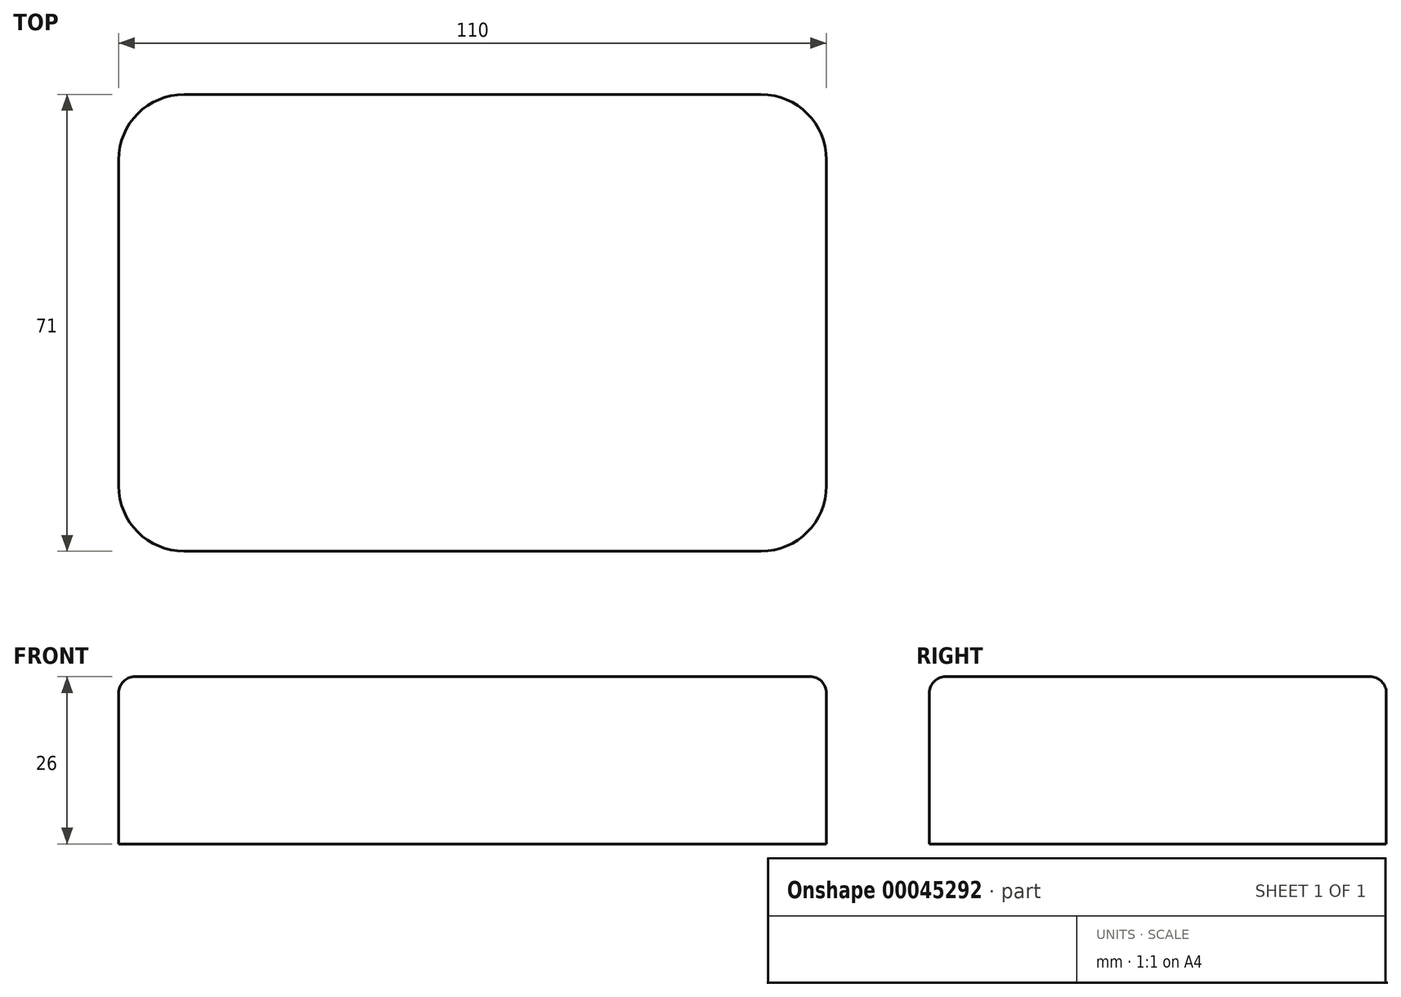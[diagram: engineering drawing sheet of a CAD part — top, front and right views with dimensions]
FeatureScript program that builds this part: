
annotation { "Feature Type Name" : "Feature", "Feature Type Description" : "" }
export const myFeature = defineFeature(function(context is Context, id is Id, definition is map)
    precondition{}
    {
        {
            var Q0;
            Q0=qCreatedBy(makeId("Top.planeOp"),FACE);
            var sketch = newSketch(context, id + "F0", { "sketchPlane" : qUnion([Q0])});
            skLineSegment(sketch, "E0.bottom", {"start": v(0, 0) * mm, "end": v(110, 0) * mm});
            skLineSegment(sketch, "E0.top", {"start": v(0, 71) * mm, "end": v(110, 71) * mm});
            skLineSegment(sketch, "E0.left", {"start": v(0, 0) * mm, "end": v(0, 71) * mm});
            skLineSegment(sketch, "E0.right", {"start": v(110, 0) * mm, "end": v(110, 71) * mm});
            skSolve(sketch);
        }
        {
            var Q0;
            Q0=makeQuery(id+"F0.imprint","IMPRINT",FACE,{"disambiguationData":[TD([[makeQuery(id+"F0.imprint","IMPRINT",EDGE,{"derivedFrom":sQuery(id+"F0.wireOp",EDGE,"E0.bottom")}),1.0]])]});
            extrude(context, id + "F1", {"entities" : qUnion([Q0]), "depth" : 26 * mm});
        }
        {
            var Q0;
            Q0=makeQuery(id+"F1.opExtrude","SWEPT_EDGE",EDGE,{"disambiguationData":[OSD([sQuery(id+"F0.wireOp",EDGE,"E0.top"),sQuery(id+"F0.wireOp",EDGE,"E0.right")])]});
            var Q1;
            Q1=makeQuery(id+"F1.opExtrude","SWEPT_EDGE",EDGE,{"disambiguationData":[OSD([sQuery(id+"F0.wireOp",EDGE,"E0.top"),sQuery(id+"F0.wireOp",EDGE,"E0.left")])]});
            var Q2;
            Q2=makeQuery(id+"F1.opExtrude","SWEPT_EDGE",EDGE,{"disambiguationData":[OSD([sQuery(id+"F0.wireOp",EDGE,"E0.bottom"),sQuery(id+"F0.wireOp",EDGE,"E0.left")])]});
            var Q3;
            Q3=makeQuery(id+"F1.opExtrude","SWEPT_EDGE",EDGE,{"disambiguationData":[OSD([sQuery(id+"F0.wireOp",EDGE,"E0.bottom"),sQuery(id+"F0.wireOp",EDGE,"E0.right")])]});
            fillet(context, id + "F2", {"entities" : qUnion([Q0, Q1, Q2, Q3]), "radius" : 10.16 * mm, "tangentPropagation" : true, "allowEdgeOverflow" : false});
        }
        {
            var Q0;
            Q0=makeQuery(id+"F1.opExtrude","CAP_FACE",FACE,{"disambiguationData":[OSD([sQuery(id+"F0.wireOp",EDGE,"E0.bottom"),sQuery(id+"F0.wireOp",EDGE,"E0.top"),sQuery(id+"F0.wireOp",EDGE,"E0.left"),sQuery(id+"F0.wireOp",EDGE,"E0.right")])],"isStart":false});
            fillet(context, id + "F3", {"entities" : qUnion([Q0]), "radius" : 2.54 * mm, "tangentPropagation" : true, "allowEdgeOverflow" : false});
        }
    });
